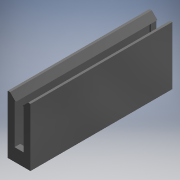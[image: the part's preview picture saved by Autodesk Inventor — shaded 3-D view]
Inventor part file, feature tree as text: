
AUTODESK INVENTOR PART (.ipt)
format: ipt  version: 2019 (Build 230136000, 136)  size: 157,184 bytes
history: native  units: mm (DEFAULTED — no unit token found)
features: extrude x6, sketch x6, plane x2, mirror x2, chamfer x1
ambient origin geometry x8: Origin, YZ Plane, XZ Plane, XY Plane, X Axis, Y Axis, Z Axis, Center Point
bodies: Solid1 (feature_tree)
feature tree (17):
  extrude  "Extrusion1"  Depth=31.75mm
  extrude  "Extrusion7"  Depth=31.75mm
  extrude  "Extrusion8"  Depth=31.75mm
  extrude  "Extrusion9"  Depth=11.43mm TaperAngle=0.0deg
  chamfer  "Chamfer1"  Distance=1.27mm
  extrude  "Extrusion10"  Depth=1.27mm
  plane  "Work Plane5"
  plane  "Work Plane6"
  mirror  "Mirror4"
  mirror  "Mirror5"
  extrude  "Extrusion11"  Depth=0.254mm TaperAngle=0.0deg
  sketch  "Sketch1"  dims[d0=5.08mm d1=31.75mm]
  sketch  "Sketch6"  dims[d2=1.5875mm d3=0.0mm d19=31.75mm]
  sketch  "Sketch7"  dims[d20=1.27mm d21=31.75mm]
  sketch  "Sketch8"  dims[d22=1.27mm d23=11.43mm d24=0.0mm]
  sketch  "Sketch9"  dims[d25=1.27mm d26=1.27mm d27=0.0mm]
  sketch  "Sketch10"  dims[d28=31.75mm d29=1.27mm d30=0.508mm d31=0.0mm d32=1.27mm d33=3.175mm d34=45.0deg d35=1.27mm d36=8.89mm d37=0.254mm d38=0.0mm d39=1.27mm d40=8.89mm d41=0.254mm d42=0.0mm]
